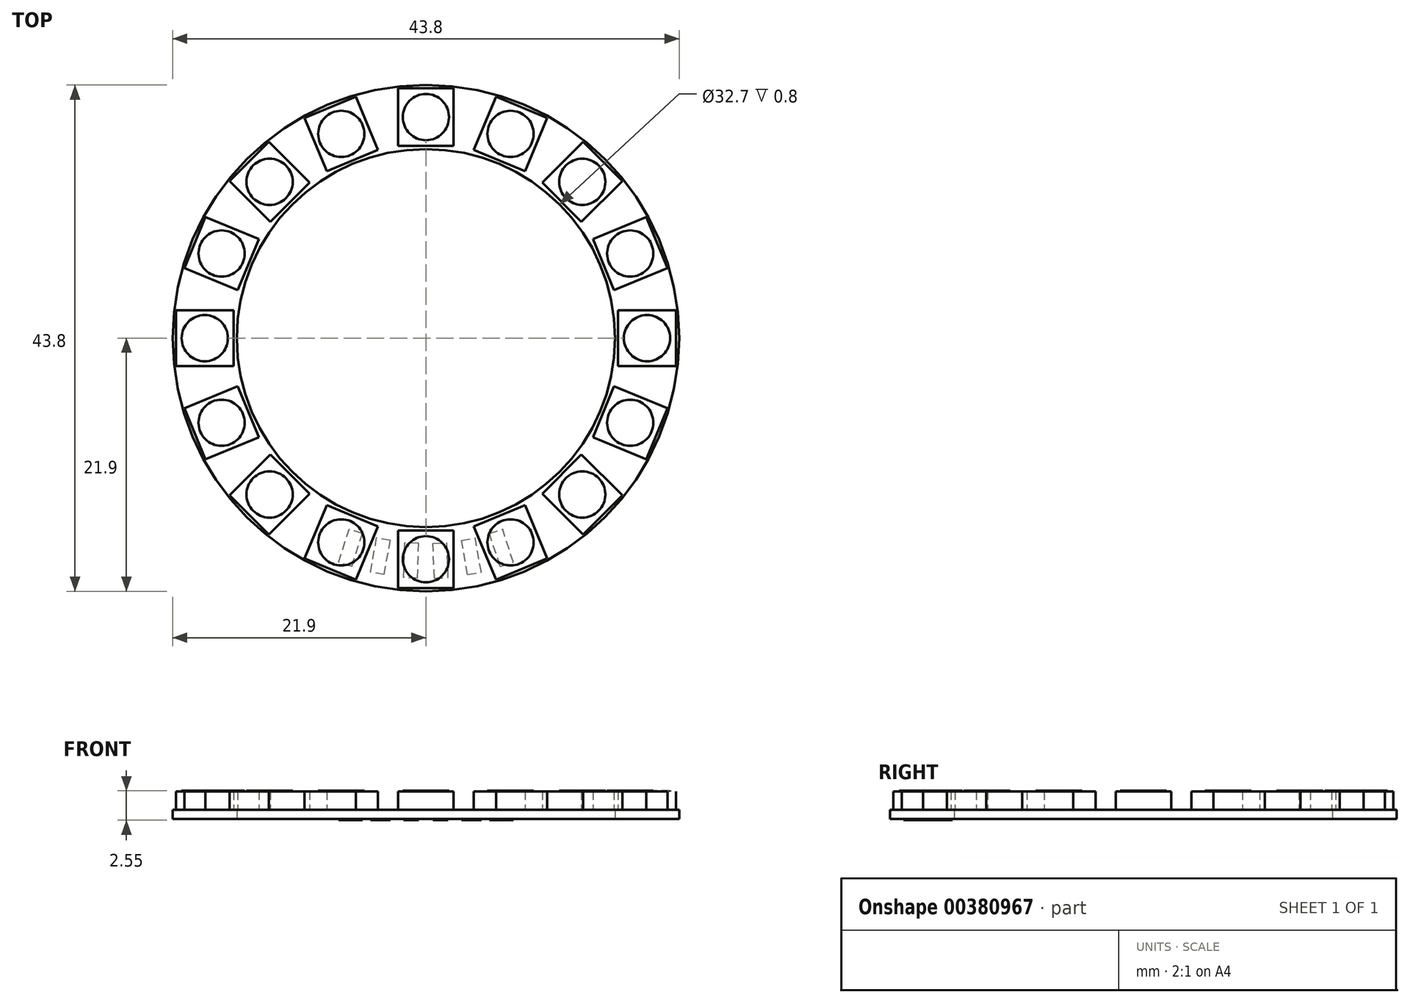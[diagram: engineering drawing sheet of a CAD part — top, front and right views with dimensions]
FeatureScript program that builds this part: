
annotation { "Feature Type Name" : "Feature", "Feature Type Description" : "" }
export const myFeature = defineFeature(function(context is Context, id is Id, definition is map)
    precondition{}
    {
        {
            var Q0;
            Q0=qCreatedBy(makeId("Top.planeOp"),FACE);
            var sketch = newSketch(context, id + "F0", { "sketchPlane" : qUnion([Q0])});
            skCircle(sketch, "E0", {"center": v(0, 0) * mm, "radius": 16.35 * mm});
            skCircle(sketch, "E1", {"center": v(0, 0) * mm, "radius": 21.9 * mm});
            skSolve(sketch);
        }
        {
            var Q0;
            Q0=makeQuery(id+"F0.imprint","IMPRINT",FACE,{"disambiguationData":[TD([[makeQuery(id+"F0.imprint","IMPRINT",EDGE,{"derivedFrom":sQuery(id+"F0.wireOp",EDGE,"E0")}),-1.0]])]});
            extrude(context, id + "F1", {"entities" : qUnion([Q0]), "depth" : 0.8 * mm});
        }
        {
            var Q0;
            Q0=makeQuery(id+"F1.opExtrude","CAP_FACE",FACE,{"disambiguationData":[OSD([sQuery(id+"F0.wireOp",EDGE,"E0"),sQuery(id+"F0.wireOp",EDGE,"E1")])],"isStart":false});
            var sketch = newSketch(context, id + "F2", { "sketchPlane" : qUnion([Q0])});
            skLineSegment(sketch, "E2", {"start": v(0, 21.9) * mm, "end": v(0, 16.35) * mm});
            skLineSegment(sketch, "E3.bottom", {"start": v(2.4, 16.62) * mm, "end": v(-2.4, 16.62) * mm});
            skLineSegment(sketch, "E3.top", {"start": v(2.4, 21.63) * mm, "end": v(-2.4, 21.63) * mm});
            skLineSegment(sketch, "E3.left", {"start": v(2.4, 16.62) * mm, "end": v(2.4, 21.63) * mm});
            skLineSegment(sketch, "E3.right", {"start": v(-2.4, 16.62) * mm, "end": v(-2.4, 21.63) * mm});
            skPoint(sketch, "E3.middle", {"position": v(0, 19.13) * mm});
            skLineSegment(sketch, "E4.1.0", {"start": v(-8.58, 14.44) * mm, "end": v(-10.5, 19.06) * mm});
            skLineSegment(sketch, "E4.1.1", {"start": v(-6.06, 20.9) * mm, "end": v(-10.5, 19.06) * mm});
            skLineSegment(sketch, "E4.1.2", {"start": v(-4.14, 16.28) * mm, "end": v(-6.06, 20.9) * mm});
            skLineSegment(sketch, "E4.1.3", {"start": v(-4.14, 16.28) * mm, "end": v(-8.58, 14.44) * mm});
            skLineSegment(sketch, "E4.2.0", {"start": v(-13.45, 10.06) * mm, "end": v(-16.99, 13.6) * mm});
            skLineSegment(sketch, "E4.2.1", {"start": v(-13.6, 16.99) * mm, "end": v(-16.99, 13.6) * mm});
            skLineSegment(sketch, "E4.2.2", {"start": v(-10.06, 13.45) * mm, "end": v(-13.6, 16.99) * mm});
            skLineSegment(sketch, "E4.2.3", {"start": v(-10.06, 13.45) * mm, "end": v(-13.45, 10.06) * mm});
            skLineSegment(sketch, "E4.3.0", {"start": v(-16.28, 4.14) * mm, "end": v(-20.9, 6.06) * mm});
            skLineSegment(sketch, "E4.3.1", {"start": v(-19.06, 10.5) * mm, "end": v(-20.9, 6.06) * mm});
            skLineSegment(sketch, "E4.3.2", {"start": v(-14.44, 8.58) * mm, "end": v(-19.06, 10.5) * mm});
            skLineSegment(sketch, "E4.3.3", {"start": v(-14.44, 8.58) * mm, "end": v(-16.28, 4.14) * mm});
            skLineSegment(sketch, "E4.4.0", {"start": v(-16.62, -2.4) * mm, "end": v(-21.63, -2.4) * mm});
            skLineSegment(sketch, "E4.4.1", {"start": v(-21.63, 2.4) * mm, "end": v(-21.63, -2.4) * mm});
            skLineSegment(sketch, "E4.4.2", {"start": v(-16.62, 2.4) * mm, "end": v(-21.63, 2.4) * mm});
            skLineSegment(sketch, "E4.4.3", {"start": v(-16.62, 2.4) * mm, "end": v(-16.62, -2.4) * mm});
            skLineSegment(sketch, "E4.5.0", {"start": v(-14.44, -8.58) * mm, "end": v(-19.06, -10.5) * mm});
            skLineSegment(sketch, "E4.5.1", {"start": v(-20.9, -6.06) * mm, "end": v(-19.06, -10.5) * mm});
            skLineSegment(sketch, "E4.5.2", {"start": v(-16.28, -4.14) * mm, "end": v(-20.9, -6.06) * mm});
            skLineSegment(sketch, "E4.5.3", {"start": v(-16.28, -4.14) * mm, "end": v(-14.44, -8.58) * mm});
            skLineSegment(sketch, "E4.6.0", {"start": v(-10.06, -13.45) * mm, "end": v(-13.6, -16.99) * mm});
            skLineSegment(sketch, "E4.6.1", {"start": v(-16.99, -13.6) * mm, "end": v(-13.6, -16.99) * mm});
            skLineSegment(sketch, "E4.6.2", {"start": v(-13.45, -10.06) * mm, "end": v(-16.99, -13.6) * mm});
            skLineSegment(sketch, "E4.6.3", {"start": v(-13.45, -10.06) * mm, "end": v(-10.06, -13.45) * mm});
            skLineSegment(sketch, "E4.7.0", {"start": v(-4.14, -16.28) * mm, "end": v(-6.06, -20.9) * mm});
            skLineSegment(sketch, "E4.7.1", {"start": v(-10.5, -19.06) * mm, "end": v(-6.06, -20.9) * mm});
            skLineSegment(sketch, "E4.7.2", {"start": v(-8.58, -14.44) * mm, "end": v(-10.5, -19.06) * mm});
            skLineSegment(sketch, "E4.7.3", {"start": v(-8.58, -14.44) * mm, "end": v(-4.14, -16.28) * mm});
            skLineSegment(sketch, "E4.8.0", {"start": v(2.4, -16.62) * mm, "end": v(2.4, -21.63) * mm});
            skLineSegment(sketch, "E4.8.1", {"start": v(-2.4, -21.63) * mm, "end": v(2.4, -21.63) * mm});
            skLineSegment(sketch, "E4.8.2", {"start": v(-2.4, -16.62) * mm, "end": v(-2.4, -21.63) * mm});
            skLineSegment(sketch, "E4.8.3", {"start": v(-2.4, -16.62) * mm, "end": v(2.4, -16.62) * mm});
            skLineSegment(sketch, "E4.9.0", {"start": v(8.58, -14.44) * mm, "end": v(10.5, -19.06) * mm});
            skLineSegment(sketch, "E4.9.1", {"start": v(6.06, -20.9) * mm, "end": v(10.5, -19.06) * mm});
            skLineSegment(sketch, "E4.9.2", {"start": v(4.14, -16.28) * mm, "end": v(6.06, -20.9) * mm});
            skLineSegment(sketch, "E4.9.3", {"start": v(4.14, -16.28) * mm, "end": v(8.58, -14.44) * mm});
            skLineSegment(sketch, "E4.10.0", {"start": v(13.45, -10.06) * mm, "end": v(16.99, -13.6) * mm});
            skLineSegment(sketch, "E4.10.1", {"start": v(13.6, -16.99) * mm, "end": v(16.99, -13.6) * mm});
            skLineSegment(sketch, "E4.10.2", {"start": v(10.06, -13.45) * mm, "end": v(13.6, -16.99) * mm});
            skLineSegment(sketch, "E4.10.3", {"start": v(10.06, -13.45) * mm, "end": v(13.45, -10.06) * mm});
            skLineSegment(sketch, "E4.11.0", {"start": v(16.28, -4.14) * mm, "end": v(20.9, -6.06) * mm});
            skLineSegment(sketch, "E4.11.1", {"start": v(19.06, -10.5) * mm, "end": v(20.9, -6.06) * mm});
            skLineSegment(sketch, "E4.11.2", {"start": v(14.44, -8.58) * mm, "end": v(19.06, -10.5) * mm});
            skLineSegment(sketch, "E4.11.3", {"start": v(14.44, -8.58) * mm, "end": v(16.28, -4.14) * mm});
            skLineSegment(sketch, "E4.12.0", {"start": v(16.62, 2.4) * mm, "end": v(21.63, 2.4) * mm});
            skLineSegment(sketch, "E4.12.1", {"start": v(21.63, -2.4) * mm, "end": v(21.63, 2.4) * mm});
            skLineSegment(sketch, "E4.12.2", {"start": v(16.62, -2.4) * mm, "end": v(21.63, -2.4) * mm});
            skLineSegment(sketch, "E4.12.3", {"start": v(16.62, -2.4) * mm, "end": v(16.62, 2.4) * mm});
            skLineSegment(sketch, "E4.13.0", {"start": v(14.44, 8.58) * mm, "end": v(19.06, 10.5) * mm});
            skLineSegment(sketch, "E4.13.1", {"start": v(20.9, 6.06) * mm, "end": v(19.06, 10.5) * mm});
            skLineSegment(sketch, "E4.13.2", {"start": v(16.28, 4.14) * mm, "end": v(20.9, 6.06) * mm});
            skLineSegment(sketch, "E4.13.3", {"start": v(16.28, 4.14) * mm, "end": v(14.44, 8.58) * mm});
            skLineSegment(sketch, "E4.14.0", {"start": v(10.06, 13.45) * mm, "end": v(13.6, 16.99) * mm});
            skLineSegment(sketch, "E4.14.1", {"start": v(16.99, 13.6) * mm, "end": v(13.6, 16.99) * mm});
            skLineSegment(sketch, "E4.14.2", {"start": v(13.45, 10.06) * mm, "end": v(16.99, 13.6) * mm});
            skLineSegment(sketch, "E4.14.3", {"start": v(13.45, 10.06) * mm, "end": v(10.06, 13.45) * mm});
            skLineSegment(sketch, "E4.15.0", {"start": v(4.14, 16.28) * mm, "end": v(6.06, 20.9) * mm});
            skLineSegment(sketch, "E4.15.1", {"start": v(10.5, 19.06) * mm, "end": v(6.06, 20.9) * mm});
            skLineSegment(sketch, "E4.15.2", {"start": v(8.58, 14.44) * mm, "end": v(10.5, 19.06) * mm});
            skLineSegment(sketch, "E4.15.3", {"start": v(8.58, 14.44) * mm, "end": v(4.14, 16.28) * mm});
            skPoint(sketch, "E4.center", {"position": v(0, 0) * mm});
            skCircle(sketch, "E5", {"center": v(0, 19.13) * mm, "radius": 2 * mm});
            skCircle(sketch, "E6.1.0", {"center": v(-7.32, 17.67) * mm, "radius": 2 * mm});
            skCircle(sketch, "E6.2.0", {"center": v(-13.52, 13.52) * mm, "radius": 2 * mm});
            skCircle(sketch, "E6.3.0", {"center": v(-17.67, 7.32) * mm, "radius": 2 * mm});
            skCircle(sketch, "E6.4.0", {"center": v(-19.13, 0) * mm, "radius": 2 * mm});
            skCircle(sketch, "E6.5.0", {"center": v(-17.67, -7.32) * mm, "radius": 2 * mm});
            skCircle(sketch, "E6.6.0", {"center": v(-13.52, -13.52) * mm, "radius": 2 * mm});
            skCircle(sketch, "E6.7.0", {"center": v(-7.32, -17.67) * mm, "radius": 2 * mm});
            skCircle(sketch, "E6.8.0", {"center": v(0, -19.13) * mm, "radius": 2 * mm});
            skCircle(sketch, "E6.9.0", {"center": v(7.32, -17.67) * mm, "radius": 2 * mm});
            skCircle(sketch, "E6.10.0", {"center": v(13.52, -13.52) * mm, "radius": 2 * mm});
            skCircle(sketch, "E6.11.0", {"center": v(17.67, -7.32) * mm, "radius": 2 * mm});
            skCircle(sketch, "E6.12.0", {"center": v(19.13, 0) * mm, "radius": 2 * mm});
            skCircle(sketch, "E6.13.0", {"center": v(17.67, 7.32) * mm, "radius": 2 * mm});
            skCircle(sketch, "E6.14.0", {"center": v(13.52, 13.52) * mm, "radius": 2 * mm});
            skCircle(sketch, "E6.15.0", {"center": v(7.32, 17.67) * mm, "radius": 2 * mm});
            skSolve(sketch);
        }
        {
            var Q0;
            Q0 = qSketchRegion(id + "F2", true);
            extrude(context, id + "F3", {"entities" : qUnion([Q0]), "operationType" : NewBodyOperationType.ADD, "depth" : 1.6 * mm});
        }
        {
            var Q0;
            Q0=makeQuery(id+"F3.boolean.opBoolean","SPLIT",FACE,{"disambiguationData":[TD([makeQuery(id+"F3.opExtrude","SWEPT_FACE",FACE,{"disambiguationData":[OSD([sQuery(id+"F2.wireOp",EDGE,"E6.3.0")])]})])],"derivedFrom":makeQuery(id+"F1.opExtrude","CAP_FACE",FACE,{"disambiguationData":[OSD([sQuery(id+"F0.wireOp",EDGE,"E0"),sQuery(id+"F0.wireOp",EDGE,"E1")])],"isStart":false})});
            var Q1;
            Q1=makeQuery(id+"F3.boolean.opBoolean","SPLIT",FACE,{"disambiguationData":[TD([makeQuery(id+"F3.opExtrude","SWEPT_FACE",FACE,{"disambiguationData":[OSD([sQuery(id+"F2.wireOp",EDGE,"E6.2.0")])]})])],"derivedFrom":makeQuery(id+"F1.opExtrude","CAP_FACE",FACE,{"disambiguationData":[OSD([sQuery(id+"F0.wireOp",EDGE,"E0"),sQuery(id+"F0.wireOp",EDGE,"E1")])],"isStart":false})});
            var Q2;
            Q2=makeQuery(id+"F3.boolean.opBoolean","SPLIT",FACE,{"disambiguationData":[TD([makeQuery(id+"F3.opExtrude","SWEPT_FACE",FACE,{"disambiguationData":[OSD([sQuery(id+"F2.wireOp",EDGE,"E6.1.0")])]})])],"derivedFrom":makeQuery(id+"F1.opExtrude","CAP_FACE",FACE,{"disambiguationData":[OSD([sQuery(id+"F0.wireOp",EDGE,"E0"),sQuery(id+"F0.wireOp",EDGE,"E1")])],"isStart":false})});
            var Q3;
            Q3=makeQuery(id+"F3.boolean.opBoolean","SPLIT",FACE,{"disambiguationData":[TD([makeQuery(id+"F3.opExtrude","SWEPT_FACE",FACE,{"disambiguationData":[OSD([sQuery(id+"F2.wireOp",EDGE,"E5")])]})])],"derivedFrom":makeQuery(id+"F1.opExtrude","CAP_FACE",FACE,{"disambiguationData":[OSD([sQuery(id+"F0.wireOp",EDGE,"E0"),sQuery(id+"F0.wireOp",EDGE,"E1")])],"isStart":false})});
            var Q4;
            Q4=makeQuery(id+"F3.boolean.opBoolean","SPLIT",FACE,{"disambiguationData":[TD([makeQuery(id+"F3.opExtrude","SWEPT_FACE",FACE,{"disambiguationData":[OSD([sQuery(id+"F2.wireOp",EDGE,"E6.15.0")])]})])],"derivedFrom":makeQuery(id+"F1.opExtrude","CAP_FACE",FACE,{"disambiguationData":[OSD([sQuery(id+"F0.wireOp",EDGE,"E0"),sQuery(id+"F0.wireOp",EDGE,"E1")])],"isStart":false})});
            var Q5;
            Q5=makeQuery(id+"F3.boolean.opBoolean","SPLIT",FACE,{"disambiguationData":[TD([makeQuery(id+"F3.opExtrude","SWEPT_FACE",FACE,{"disambiguationData":[OSD([sQuery(id+"F2.wireOp",EDGE,"E6.4.0")])]})])],"derivedFrom":makeQuery(id+"F1.opExtrude","CAP_FACE",FACE,{"disambiguationData":[OSD([sQuery(id+"F0.wireOp",EDGE,"E0"),sQuery(id+"F0.wireOp",EDGE,"E1")])],"isStart":false})});
            var Q6;
            Q6=makeQuery(id+"F3.boolean.opBoolean","SPLIT",FACE,{"disambiguationData":[TD([makeQuery(id+"F3.opExtrude","SWEPT_FACE",FACE,{"disambiguationData":[OSD([sQuery(id+"F2.wireOp",EDGE,"E6.5.0")])]})])],"derivedFrom":makeQuery(id+"F1.opExtrude","CAP_FACE",FACE,{"disambiguationData":[OSD([sQuery(id+"F0.wireOp",EDGE,"E0"),sQuery(id+"F0.wireOp",EDGE,"E1")])],"isStart":false})});
            var Q7;
            Q7=makeQuery(id+"F3.boolean.opBoolean","SPLIT",FACE,{"disambiguationData":[TD([makeQuery(id+"F3.opExtrude","SWEPT_FACE",FACE,{"disambiguationData":[OSD([sQuery(id+"F2.wireOp",EDGE,"E6.6.0")])]})])],"derivedFrom":makeQuery(id+"F1.opExtrude","CAP_FACE",FACE,{"disambiguationData":[OSD([sQuery(id+"F0.wireOp",EDGE,"E0"),sQuery(id+"F0.wireOp",EDGE,"E1")])],"isStart":false})});
            var Q8;
            Q8=makeQuery(id+"F3.boolean.opBoolean","SPLIT",FACE,{"disambiguationData":[TD([makeQuery(id+"F3.opExtrude","SWEPT_FACE",FACE,{"disambiguationData":[OSD([sQuery(id+"F2.wireOp",EDGE,"E6.7.0")])]})])],"derivedFrom":makeQuery(id+"F1.opExtrude","CAP_FACE",FACE,{"disambiguationData":[OSD([sQuery(id+"F0.wireOp",EDGE,"E0"),sQuery(id+"F0.wireOp",EDGE,"E1")])],"isStart":false})});
            var Q9;
            Q9=makeQuery(id+"F3.boolean.opBoolean","SPLIT",FACE,{"disambiguationData":[TD([makeQuery(id+"F3.opExtrude","SWEPT_FACE",FACE,{"disambiguationData":[OSD([sQuery(id+"F2.wireOp",EDGE,"E6.8.0")])]})])],"derivedFrom":makeQuery(id+"F1.opExtrude","CAP_FACE",FACE,{"disambiguationData":[OSD([sQuery(id+"F0.wireOp",EDGE,"E0"),sQuery(id+"F0.wireOp",EDGE,"E1")])],"isStart":false})});
            var Q10;
            Q10=makeQuery(id+"F3.boolean.opBoolean","SPLIT",FACE,{"disambiguationData":[TD([makeQuery(id+"F3.opExtrude","SWEPT_FACE",FACE,{"disambiguationData":[OSD([sQuery(id+"F2.wireOp",EDGE,"E6.9.0")])]})])],"derivedFrom":makeQuery(id+"F1.opExtrude","CAP_FACE",FACE,{"disambiguationData":[OSD([sQuery(id+"F0.wireOp",EDGE,"E0"),sQuery(id+"F0.wireOp",EDGE,"E1")])],"isStart":false})});
            var Q11;
            Q11=makeQuery(id+"F3.boolean.opBoolean","SPLIT",FACE,{"disambiguationData":[TD([makeQuery(id+"F3.opExtrude","SWEPT_FACE",FACE,{"disambiguationData":[OSD([sQuery(id+"F2.wireOp",EDGE,"E6.10.0")])]})])],"derivedFrom":makeQuery(id+"F1.opExtrude","CAP_FACE",FACE,{"disambiguationData":[OSD([sQuery(id+"F0.wireOp",EDGE,"E0"),sQuery(id+"F0.wireOp",EDGE,"E1")])],"isStart":false})});
            var Q12;
            Q12=makeQuery(id+"F3.boolean.opBoolean","SPLIT",FACE,{"disambiguationData":[TD([makeQuery(id+"F3.opExtrude","SWEPT_FACE",FACE,{"disambiguationData":[OSD([sQuery(id+"F2.wireOp",EDGE,"E6.11.0")])]})])],"derivedFrom":makeQuery(id+"F1.opExtrude","CAP_FACE",FACE,{"disambiguationData":[OSD([sQuery(id+"F0.wireOp",EDGE,"E0"),sQuery(id+"F0.wireOp",EDGE,"E1")])],"isStart":false})});
            var Q13;
            Q13=makeQuery(id+"F3.boolean.opBoolean","SPLIT",FACE,{"disambiguationData":[TD([makeQuery(id+"F3.opExtrude","SWEPT_FACE",FACE,{"disambiguationData":[OSD([sQuery(id+"F2.wireOp",EDGE,"E6.12.0")])]})])],"derivedFrom":makeQuery(id+"F1.opExtrude","CAP_FACE",FACE,{"disambiguationData":[OSD([sQuery(id+"F0.wireOp",EDGE,"E0"),sQuery(id+"F0.wireOp",EDGE,"E1")])],"isStart":false})});
            var Q14;
            Q14=makeQuery(id+"F3.boolean.opBoolean","SPLIT",FACE,{"disambiguationData":[TD([makeQuery(id+"F3.opExtrude","SWEPT_FACE",FACE,{"disambiguationData":[OSD([sQuery(id+"F2.wireOp",EDGE,"E6.14.0")])]})])],"derivedFrom":makeQuery(id+"F1.opExtrude","CAP_FACE",FACE,{"disambiguationData":[OSD([sQuery(id+"F0.wireOp",EDGE,"E0"),sQuery(id+"F0.wireOp",EDGE,"E1")])],"isStart":false})});
            var Q15;
            Q15=makeQuery(id+"F3.boolean.opBoolean","SPLIT",FACE,{"disambiguationData":[TD([makeQuery(id+"F3.opExtrude","SWEPT_FACE",FACE,{"disambiguationData":[OSD([sQuery(id+"F2.wireOp",EDGE,"E6.13.0")])]})])],"derivedFrom":makeQuery(id+"F1.opExtrude","CAP_FACE",FACE,{"disambiguationData":[OSD([sQuery(id+"F0.wireOp",EDGE,"E0"),sQuery(id+"F0.wireOp",EDGE,"E1")])],"isStart":false})});
            extrude(context, id + "F4", {"entities" : qUnion([Q0, Q1, Q2, Q3, Q4, Q5, Q6, Q7, Q8, Q9, Q10, Q11, Q12, Q13, Q14, Q15]), "operationType" : NewBodyOperationType.ADD, "depth" : 1.65 * mm});
        }
        {
            var Q0;
            Q0=makeQuery(id+"F1.opExtrude","CAP_FACE",FACE,{"disambiguationData":[OSD([sQuery(id+"F0.wireOp",EDGE,"E0"),sQuery(id+"F0.wireOp",EDGE,"E1")])],"isStart":true});
            var sketch = newSketch(context, id + "F5", { "sketchPlane" : qUnion([Q0])});
            skLineSegment(sketch, "E7", {"start": v(0, 0) * mm, "end": v(5.49, 16.9) * mm, "construction": true});
            skLineSegment(sketch, "E8.bottom", {"start": v(6.42, 19.75) * mm, "end": v(7.56, 19.38) * mm});
            skLineSegment(sketch, "E8.top", {"start": v(5.49, 16.9) * mm, "end": v(6.63, 16.52) * mm});
            skLineSegment(sketch, "E8.left", {"start": v(6.42, 19.75) * mm, "end": v(5.49, 16.9) * mm});
            skLineSegment(sketch, "E8.right", {"start": v(7.56, 19.38) * mm, "end": v(6.63, 16.52) * mm});
            skLineSegment(sketch, "E9", {"start": v(0, 0) * mm, "end": v(0.62, 17.75) * mm, "construction": true});
            skLineSegment(sketch, "E10.bottom", {"start": v(0.72, 20.75) * mm, "end": v(1.92, 20.7) * mm});
            skLineSegment(sketch, "E10.top", {"start": v(0.62, 17.75) * mm, "end": v(1.82, 17.71) * mm});
            skLineSegment(sketch, "E10.left", {"start": v(0.72, 20.75) * mm, "end": v(0.62, 17.75) * mm});
            skLineSegment(sketch, "E10.right", {"start": v(1.92, 20.7) * mm, "end": v(1.82, 17.71) * mm});
            skLineSegment(sketch, "E11", {"start": v(0, 0) * mm, "end": v(3.08, 17.5) * mm, "construction": true});
            skLineSegment(sketch, "E12.bottom", {"start": v(3.6, 20.45) * mm, "end": v(4.79, 20.24) * mm});
            skLineSegment(sketch, "E12.top", {"start": v(3.08, 17.5) * mm, "end": v(4.27, 17.29) * mm});
            skLineSegment(sketch, "E12.left", {"start": v(3.6, 20.45) * mm, "end": v(3.08, 17.5) * mm});
            skLineSegment(sketch, "E12.right", {"start": v(4.79, 20.24) * mm, "end": v(4.27, 17.29) * mm});
            skLineSegment(sketch, "E13.MirrorCS", {"start": v(-0.72, 20.75) * mm, "end": v(-1.92, 20.7) * mm});
            skLineSegment(sketch, "E14.MirrorCS", {"start": v(-0.62, 17.75) * mm, "end": v(-1.82, 17.71) * mm});
            skLineSegment(sketch, "E15.MirrorCS", {"start": v(-1.92, 20.7) * mm, "end": v(-1.82, 17.71) * mm});
            skLineSegment(sketch, "E16.MirrorCS", {"start": v(0, 0) * mm, "end": v(-0.62, 17.75) * mm, "construction": true});
            skLineSegment(sketch, "E17.MirrorCS", {"start": v(-3.6, 20.45) * mm, "end": v(-4.79, 20.24) * mm});
            skLineSegment(sketch, "E18.MirrorCS", {"start": v(-4.79, 20.24) * mm, "end": v(-4.27, 17.29) * mm});
            skLineSegment(sketch, "E19.MirrorCS", {"start": v(-3.08, 17.5) * mm, "end": v(-4.27, 17.29) * mm});
            skLineSegment(sketch, "E20.MirrorCS", {"start": v(-6.42, 19.75) * mm, "end": v(-7.56, 19.38) * mm});
            skLineSegment(sketch, "E21.MirrorCS", {"start": v(-7.56, 19.38) * mm, "end": v(-6.63, 16.52) * mm});
            skLineSegment(sketch, "E22.MirrorCS", {"start": v(-5.49, 16.9) * mm, "end": v(-6.63, 16.52) * mm});
            skLineSegment(sketch, "E23.MirrorCS", {"start": v(-6.42, 19.75) * mm, "end": v(-5.49, 16.9) * mm});
            skLineSegment(sketch, "E24.MirrorCS", {"start": v(-3.6, 20.45) * mm, "end": v(-3.08, 17.5) * mm});
            skLineSegment(sketch, "E25.MirrorCS", {"start": v(-0.72, 20.75) * mm, "end": v(-0.62, 17.75) * mm});
            skSolve(sketch);
        }
        {
            var Q0;
            Q0 = qSketchRegion(id + "F5", true);
            extrude(context, id + "F6", {"entities" : qUnion([Q0]), "operationType" : NewBodyOperationType.ADD, "depth" : .1 * mm});
        }
    });
